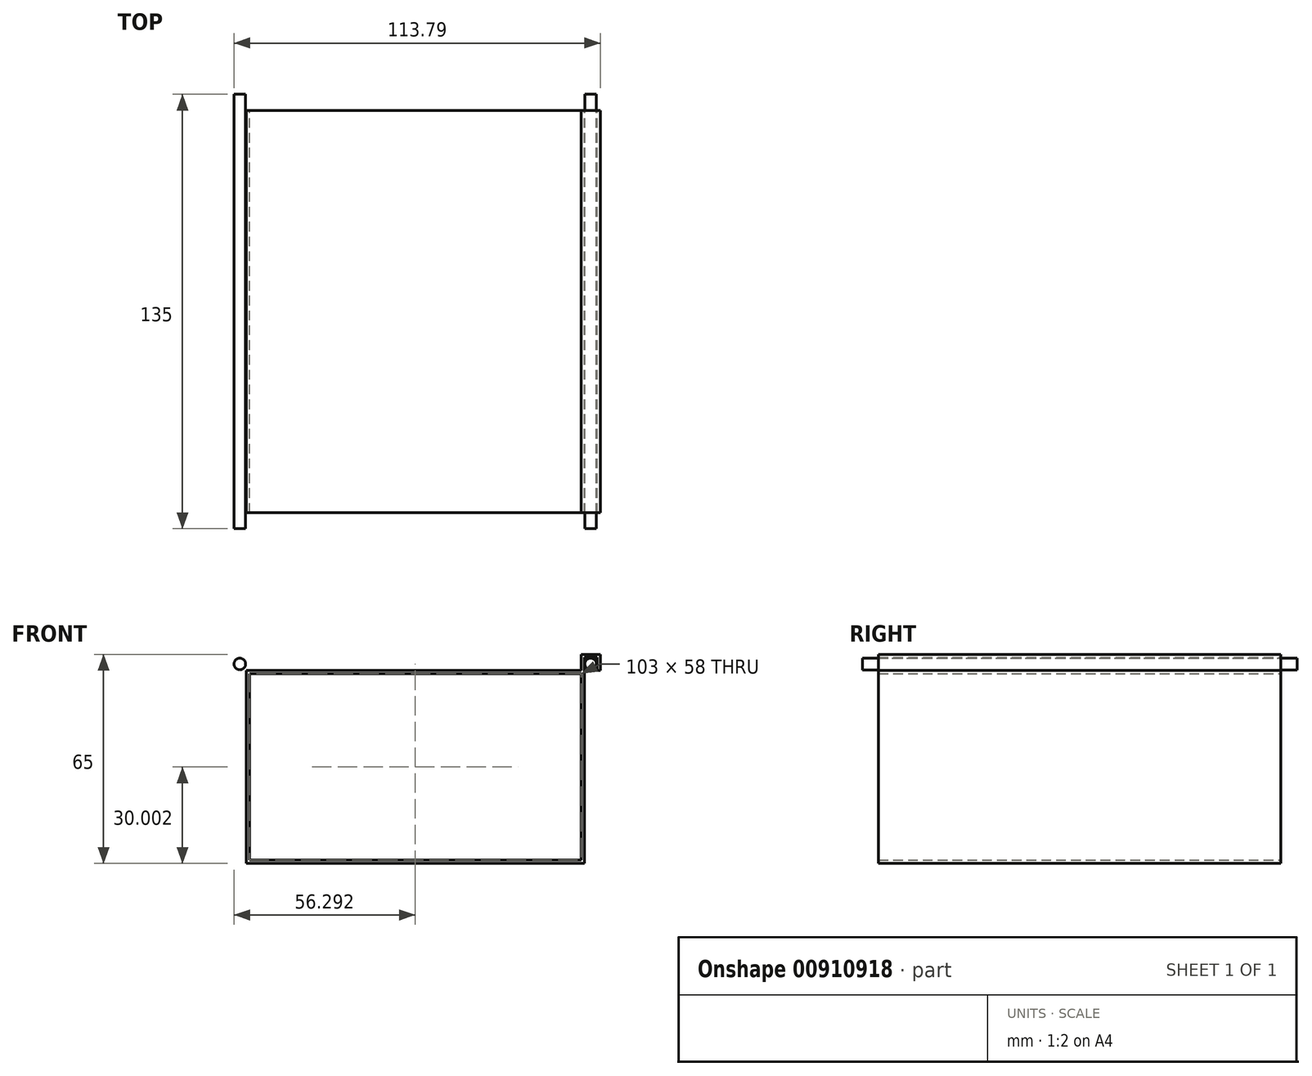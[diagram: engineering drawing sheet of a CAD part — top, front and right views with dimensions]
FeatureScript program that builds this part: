
annotation { "Feature Type Name" : "Feature", "Feature Type Description" : "" }
export const myFeature = defineFeature(function(context is Context, id is Id, definition is map)
    precondition{}
    {
        {
            var Q0;
            Q0=qCreatedBy(makeId("Front.planeOp"),FACE);
            var sketch = newSketch(context, id + "F0", { "sketchPlane" : qUnion([Q0])});
            skLineSegment(sketch, "E0.bottom", {"start": v(-58.07, 19.6) * mm, "end": v(46.93, 19.6) * mm});
            skLineSegment(sketch, "E0.top", {"start": v(-58.07, -40.4) * mm, "end": v(46.93, -40.4) * mm});
            skLineSegment(sketch, "E0.left", {"start": v(-58.07, 19.6) * mm, "end": v(-58.07, -40.4) * mm});
            skLineSegment(sketch, "E0.right", {"start": v(46.93, 19.6) * mm, "end": v(46.93, -40.4) * mm});
            skLineSegment(sketch, "E1", {"start": v(-58.07, -40.4) * mm, "end": v(-58.07, -10.4) * mm});
            skLineSegment(sketch, "E2.bottom", {"start": v(-58.07, 19.6) * mm, "end": v(-57.07, 19.6) * mm});
            skLineSegment(sketch, "E2.top", {"start": v(-58.07, 24.6) * mm, "end": v(-57.07, 24.6) * mm});
            skLineSegment(sketch, "E2.right", {"start": v(-57.07, 19.6) * mm, "end": v(-57.07, 24.6) * mm});
            skLineSegment(sketch, "E3.bottom", {"start": v(-58.07, 24.6) * mm, "end": v(-63.07, 24.6) * mm});
            skLineSegment(sketch, "E3.right", {"start": v(-63.07, 24.6) * mm, "end": v(-63.07, 19.6) * mm});
            skLineSegment(sketch, "E4", {"start": v(-63.07, 19.6) * mm, "end": v(-62.07, 19.6) * mm});
            skLineSegment(sketch, "E5", {"start": v(-63.07, 24.6) * mm, "end": v(-63.07, 23.6) * mm});
            skLineSegment(sketch, "E6", {"start": v(-62.07, 19.6) * mm, "end": v(-62.07, 23.6) * mm});
            skLineSegment(sketch, "E7", {"start": v(-62.07, 23.6) * mm, "end": v(-58.07, 23.6) * mm});
            skLineSegment(sketch, "E8", {"start": v(-58.07, 23.6) * mm, "end": v(-58.07, 19.6) * mm});
            skLineSegment(sketch, "E9", {"start": v(-58.07, -40.4) * mm, "end": v(-5.57, -40.4) * mm});
            skLineSegment(sketch, "E10", {"start": v(-5.57, -40.4) * mm, "end": v(-5.57, 19.6) * mm});
            skLineSegment(sketch, "E11.MirrorCS", {"start": v(51.93, 19.6) * mm, "end": v(50.93, 19.6) * mm});
            skLineSegment(sketch, "E12.MirrorCS", {"start": v(50.93, 23.6) * mm, "end": v(46.93, 23.6) * mm});
            skLineSegment(sketch, "E13.MirrorCS", {"start": v(46.93, 23.6) * mm, "end": v(46.93, 19.6) * mm});
            skLineSegment(sketch, "E14.MirrorCS", {"start": v(46.93, 19.6) * mm, "end": v(45.93, 19.6) * mm});
            skLineSegment(sketch, "E15.MirrorCS", {"start": v(51.93, 24.6) * mm, "end": v(51.93, 23.6) * mm});
            skLineSegment(sketch, "E16.MirrorCS", {"start": v(51.93, 24.6) * mm, "end": v(51.93, 19.6) * mm});
            skLineSegment(sketch, "E17.MirrorCS", {"start": v(46.93, 24.6) * mm, "end": v(51.93, 24.6) * mm});
            skLineSegment(sketch, "E18.MirrorCS", {"start": v(46.93, 24.6) * mm, "end": v(45.93, 24.6) * mm});
            skLineSegment(sketch, "E19.MirrorCS", {"start": v(45.93, 19.6) * mm, "end": v(45.93, 24.6) * mm});
            skLineSegment(sketch, "E20.MirrorCS", {"start": v(50.93, 19.6) * mm, "end": v(50.93, 23.6) * mm});
            skSolve(sketch);
        }
        {
            var Q0;
            Q0=makeQuery(id+"F0.imprint","IMPRINT",FACE,{"disambiguationData":[TD([[makeQuery(id+"F0.imprint","IMPRINT",EDGE,{"derivedFrom":sQuery(id+"F0.wireOp",EDGE,"E2.bottom")}),1.0]])]});
            var Q1;
            Q1=makeQuery(id+"F0.imprint","IMPRINT",FACE,{"disambiguationData":[TD([[makeQuery(id+"F0.imprint","IMPRINT",EDGE,{"derivedFrom":sQuery(id+"F0.wireOp",EDGE,"E0.top")}),1.0]])]});
            var Q2;
            {var subQ0=sQuery(id+"F0.wireOp",EDGE,"E11.MirrorCS");Q2=makeQuery(id+"F0.imprint","IMPRINT",FACE,{"disambiguationData":[TD([[makeQuery(id+"F0.imprint","IMPRINT",EDGE,{"derivedFrom":subQ0}),-1.0]])]});}
            var Q3;
            Q3=makeQuery(id+"F0.imprint","IMPRINT",FACE,{"disambiguationData":[TD([[makeQuery(id+"F0.imprint","IMPRINT",EDGE,{"derivedFrom":sQuery(id+"F0.wireOp",EDGE,"E0.left")}),1.0]])]});
            extrude(context, id + "F1", {"entities" : qUnion([Q0, Q1, Q2, Q3]), "depth" : 125 * mm, "offsetDistance" : 25 * mm});
        }
        {
            var Q0;
            Q0=makeQuery(id+"F1.opExtrude","CAP_FACE",FACE,{"disambiguationData":[OSD([sQuery(id+"F0.wireOp",EDGE,"E0.bottom"),sQuery(id+"F0.wireOp",EDGE,"E0.top"),sQuery(id+"F0.wireOp",EDGE,"E0.left"),sQuery(id+"F0.wireOp",EDGE,"E0.right"),sQuery(id+"F0.wireOp",EDGE,"E1"),sQuery(id+"F0.wireOp",EDGE,"E2.top"),sQuery(id+"F0.wireOp",EDGE,"E2.right"),sQuery(id+"F0.wireOp",EDGE,"E3.bottom"),sQuery(id+"F0.wireOp",EDGE,"E3.right"),sQuery(id+"F0.wireOp",EDGE,"E4"),sQuery(id+"F0.wireOp",EDGE,"E5"),sQuery(id+"F0.wireOp",EDGE,"E6"),sQuery(id+"F0.wireOp",EDGE,"E7"),sQuery(id+"F0.wireOp",EDGE,"E8"),sQuery(id+"F0.wireOp",EDGE,"E9"),sQuery(id+"F0.wireOp",EDGE,"E11.MirrorCS"),sQuery(id+"F0.wireOp",EDGE,"E12.MirrorCS"),sQuery(id+"F0.wireOp",EDGE,"E13.MirrorCS"),sQuery(id+"F0.wireOp",EDGE,"E16.MirrorCS"),sQuery(id+"F0.wireOp",EDGE,"E17.MirrorCS"),sQuery(id+"F0.wireOp",EDGE,"E18.MirrorCS"),sQuery(id+"F0.wireOp",EDGE,"E19.MirrorCS"),sQuery(id+"F0.wireOp",EDGE,"E20.MirrorCS")])],"isStart":false});
            var Q1;
            Q1=makeQuery(id+"F1.opExtrude","CAP_FACE",FACE,{"disambiguationData":[OSD([sQuery(id+"F0.wireOp",EDGE,"E0.bottom"),sQuery(id+"F0.wireOp",EDGE,"E0.top"),sQuery(id+"F0.wireOp",EDGE,"E0.left"),sQuery(id+"F0.wireOp",EDGE,"E0.right"),sQuery(id+"F0.wireOp",EDGE,"E1"),sQuery(id+"F0.wireOp",EDGE,"E2.top"),sQuery(id+"F0.wireOp",EDGE,"E2.right"),sQuery(id+"F0.wireOp",EDGE,"E3.bottom"),sQuery(id+"F0.wireOp",EDGE,"E3.right"),sQuery(id+"F0.wireOp",EDGE,"E4"),sQuery(id+"F0.wireOp",EDGE,"E5"),sQuery(id+"F0.wireOp",EDGE,"E6"),sQuery(id+"F0.wireOp",EDGE,"E7"),sQuery(id+"F0.wireOp",EDGE,"E8"),sQuery(id+"F0.wireOp",EDGE,"E9"),sQuery(id+"F0.wireOp",EDGE,"E11.MirrorCS"),sQuery(id+"F0.wireOp",EDGE,"E12.MirrorCS"),sQuery(id+"F0.wireOp",EDGE,"E13.MirrorCS"),sQuery(id+"F0.wireOp",EDGE,"E16.MirrorCS"),sQuery(id+"F0.wireOp",EDGE,"E17.MirrorCS"),sQuery(id+"F0.wireOp",EDGE,"E18.MirrorCS"),sQuery(id+"F0.wireOp",EDGE,"E19.MirrorCS"),sQuery(id+"F0.wireOp",EDGE,"E20.MirrorCS")])],"isStart":true});
            shell(context, id + "F2", {"entities" : qUnion([Q0, Q1]), "thickness" : 1 * mm});
        }
        {
            var Q0;
            Q0=qCreatedBy(makeId("Front.planeOp"),FACE);
            var sketch = newSketch(context, id + "F3", { "sketchPlane" : qUnion([Q0])});
            skCircle(sketch, "E21", {"center": v(48.92, 21.58) * mm, "radius": 1.8 * mm});
            skCircle(sketch, "E22.MirrorC", {"center": v(-60.06, 21.58) * mm, "radius": 1.8 * mm});
            skSolve(sketch);
        }
        {
            var Q0;
            Q0 = qSketchRegion(id + "F3", true);
            extrude(context, id + "F4", {"entities" : qUnion([Q0]), "depth" : 135 * mm, "offsetDistance" : 25 * mm});
        }
        {
            var Q0;
            Q0=makeQuery(id+"F4.opExtrude","SWEPT_BODY",BODY,{"disambiguationData":[OSD([sQuery(id+"F3.wireOp",EDGE,"E21")])]});
            var Q1;
            Q1=makeQuery(id+"F4.opExtrude","SWEPT_BODY",BODY,{"disambiguationData":[OSD([sQuery(id+"F3.wireOp",EDGE,"E22.MirrorC")])]});
            transform(context, id + "F5", {"entities" : qUnion([Q0, Q1]), "transformType" : TransformType.TRANSLATION_3D, "dx" : 0 * mm, "dy" : 5 * mm, "dz" : 0 * mm, "makeCopy" : false});
        }
        {
            var Q0;
            Q0=qCreatedBy(makeId("Front.planeOp"),FACE);
            var sketch = newSketch(context, id + "F6", { "sketchPlane" : qUnion([Q0])});
            skCircle(sketch, "E23", {"center": v(0, 36.41) * mm, "radius": 0.38 * mm});
            skSolve(sketch);
        }
        {
            var Q0;
            Q0=sQuery(id+"F6.wireOp",EDGE,"E23");
            extrude(context, id + "F7", {"bodyType" : ToolBodyType.SURFACE, "surfaceEntities" : qUnion([Q0]), "depth" : 25 * mm, "offsetDistance" : 25 * mm});
        }
    });
